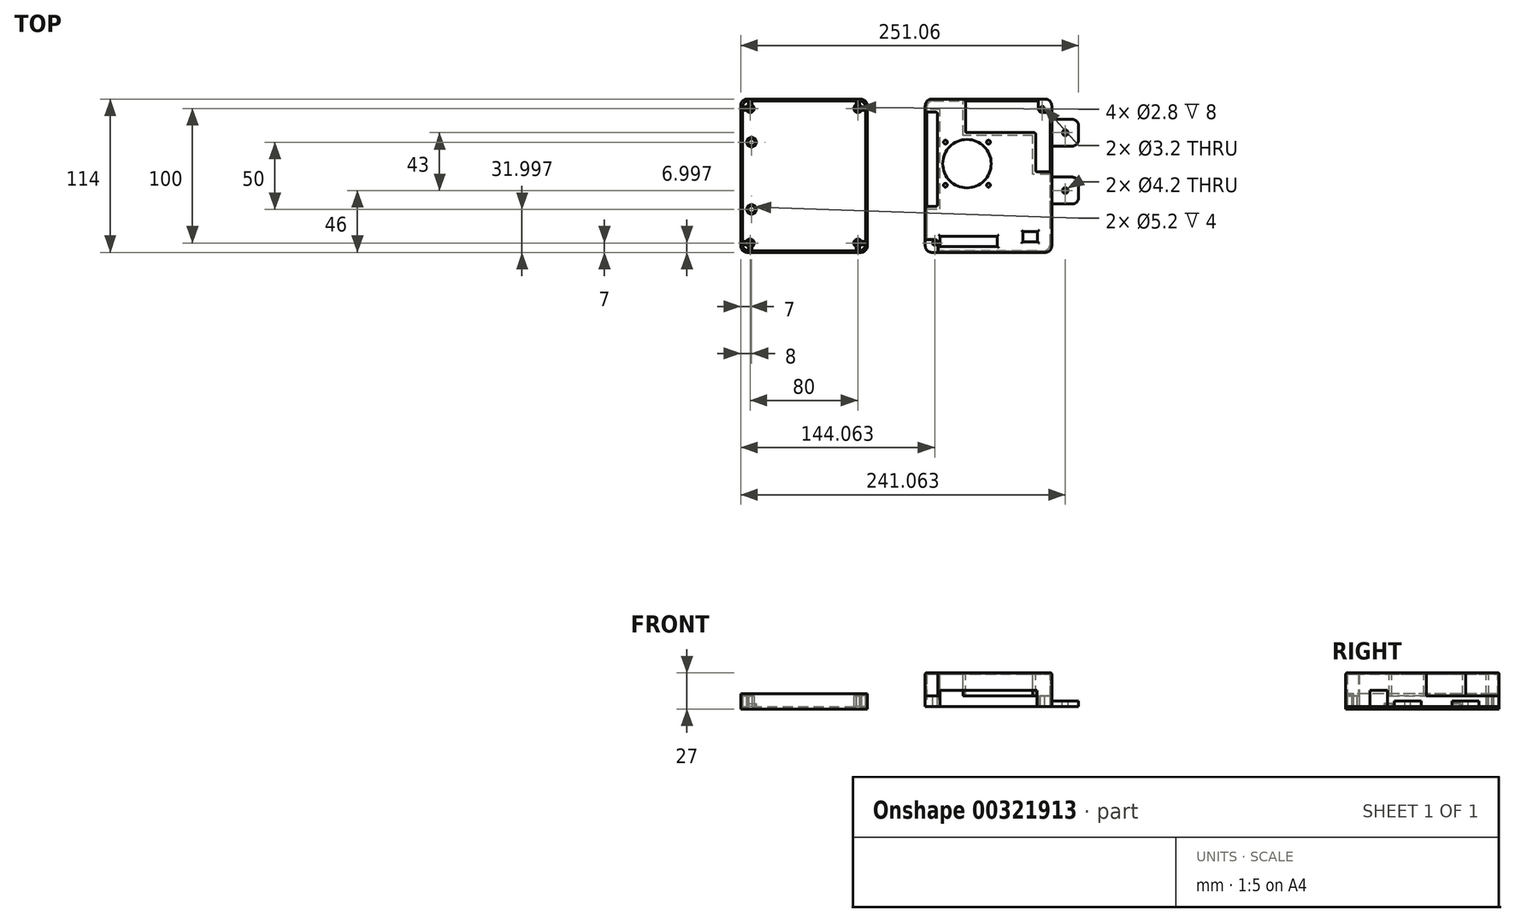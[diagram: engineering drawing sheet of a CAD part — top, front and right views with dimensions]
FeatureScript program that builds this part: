
annotation { "Feature Type Name" : "Feature", "Feature Type Description" : "" }
export const myFeature = defineFeature(function(context is Context, id is Id, definition is map)
    precondition{}
    {
        {
            var Q0;
            Q0=qCreatedBy(makeId("Top.planeOp"),FACE);
            var sketch = newSketch(context, id + "F0", { "sketchPlane" : qUnion([Q0])});
            skLineSegment(sketch, "E0.bottom", {"start": v(-88.3, 58.87) * mm, "end": v(5.7, 58.87) * mm});
            skLineSegment(sketch, "E0.top", {"start": v(-88.3, -55.13) * mm, "end": v(5.7, -55.13) * mm});
            skLineSegment(sketch, "E0.left", {"start": v(-88.3, 58.87) * mm, "end": v(-88.3, -55.13) * mm});
            skLineSegment(sketch, "E0.right", {"start": v(5.7, 58.87) * mm, "end": v(5.7, -55.13) * mm});
            skCircle(sketch, "E1", {"center": v(-81.3, 51.87) * mm, "radius": 1.4 * mm});
            skCircle(sketch, "E2", {"center": v(-81.3, -48.13) * mm, "radius": 1.4 * mm});
            skCircle(sketch, "E3", {"center": v(-1.3, -48.13) * mm, "radius": 1.4 * mm});
            skCircle(sketch, "E4", {"center": v(-1.3, 51.87) * mm, "radius": 1.4 * mm});
            skLineSegment(sketch, "E5", {"start": v(-87.1, 57.67) * mm, "end": v(4.5, 57.67) * mm});
            skLineSegment(sketch, "E6", {"start": v(-87.1, 57.67) * mm, "end": v(-87.1, -53.93) * mm});
            skLineSegment(sketch, "E7", {"start": v(-87.1, -53.93) * mm, "end": v(4.5, -53.93) * mm});
            skLineSegment(sketch, "E8", {"start": v(4.5, -53.93) * mm, "end": v(4.5, 57.67) * mm});
            skCircle(sketch, "E9", {"center": v(-81.3, 51.87) * mm, "radius": 3 * mm});
            skCircle(sketch, "E10", {"center": v(-1.3, 51.87) * mm, "radius": 3 * mm});
            skCircle(sketch, "E11", {"center": v(-81.3, -48.13) * mm, "radius": 3 * mm});
            skCircle(sketch, "E12", {"center": v(-1.3, -48.13) * mm, "radius": 3 * mm});
            skLineSegment(sketch, "E13", {"start": v(-87.1, 53.17) * mm, "end": v(-84, 53.17) * mm});
            skLineSegment(sketch, "E14", {"start": v(-87.1, 50.67) * mm, "end": v(-84, 50.67) * mm});
            skLineSegment(sketch, "E15", {"start": v(-82.6, 57.67) * mm, "end": v(-82.6, 54.57) * mm});
            skLineSegment(sketch, "E16", {"start": v(-80.1, 57.67) * mm, "end": v(-80.1, 54.62) * mm});
            skLineSegment(sketch, "E17", {"start": v(-2.5, 54.62) * mm, "end": v(-2.5, 57.67) * mm});
            skLineSegment(sketch, "E18", {"start": v(0, 57.67) * mm, "end": v(0, 54.57) * mm});
            skLineSegment(sketch, "E19", {"start": v(4.5, 53.17) * mm, "end": v(1.4, 53.17) * mm});
            skLineSegment(sketch, "E20", {"start": v(1.45, 50.67) * mm, "end": v(4.5, 50.67) * mm});
            skLineSegment(sketch, "E21", {"start": v(-87.1, -46.93) * mm, "end": v(-84.05, -46.93) * mm});
            skLineSegment(sketch, "E22", {"start": v(-87.1, -49.43) * mm, "end": v(-84, -49.43) * mm});
            skLineSegment(sketch, "E23", {"start": v(-82.6, -53.93) * mm, "end": v(-82.6, -50.84) * mm});
            skLineSegment(sketch, "E24", {"start": v(-80.1, -53.93) * mm, "end": v(-80.1, -50.88) * mm});
            skLineSegment(sketch, "E25", {"start": v(-2.5, -53.93) * mm, "end": v(-2.5, -50.88) * mm});
            skLineSegment(sketch, "E26", {"start": v(0, -53.93) * mm, "end": v(0, -50.84) * mm});
            skLineSegment(sketch, "E27", {"start": v(4.5, -49.43) * mm, "end": v(1.4, -49.43) * mm});
            skLineSegment(sketch, "E28", {"start": v(4.5, -46.93) * mm, "end": v(1.45, -46.93) * mm});
            skSolve(sketch);
        }
        {
            var Q0;
            Q0=makeQuery(id+"F0.imprint","IMPRINT",FACE,{"disambiguationData":[TD([[makeQuery(id+"F0.imprint","IMPRINT",EDGE,{"derivedFrom":sQuery(id+"F0.wireOp",EDGE,"E1")}),-1.0]])]});
            var Q1;
            Q1=makeQuery(id+"F0.imprint","IMPRINT",FACE,{"disambiguationData":[TD([[makeQuery(id+"F0.imprint","IMPRINT",EDGE,{"derivedFrom":sQuery(id+"F0.wireOp",EDGE,"E0.bottom")}),-1.0]])]});
            var Q2;
            Q2=makeQuery(id+"F0.imprint","IMPRINT",FACE,{"disambiguationData":[TD([[makeQuery(id+"F0.imprint","IMPRINT",EDGE,{"derivedFrom":sQuery(id+"F0.wireOp",EDGE,"E1")}),1.0]])]});
            var Q3;
            Q3=makeQuery(id+"F0.imprint","IMPRINT",FACE,{"disambiguationData":[TD([[makeQuery(id+"F0.imprint","IMPRINT",EDGE,{"derivedFrom":sQuery(id+"F0.wireOp",EDGE,"E4")}),1.0]])]});
            var Q4;
            Q4=makeQuery(id+"F0.imprint","IMPRINT",FACE,{"disambiguationData":[TD([[makeQuery(id+"F0.imprint","IMPRINT",EDGE,{"derivedFrom":sQuery(id+"F0.wireOp",EDGE,"E3")}),1.0]])]});
            var Q5;
            Q5=makeQuery(id+"F0.imprint","IMPRINT",FACE,{"disambiguationData":[TD([[makeQuery(id+"F0.imprint","IMPRINT",EDGE,{"derivedFrom":sQuery(id+"F0.wireOp",EDGE,"E2")}),1.0]])]});
            var Q6;
            Q6=makeQuery(id+"F0.imprint","IMPRINT",FACE,{"disambiguationData":[TD([[makeQuery(id+"F0.imprint","IMPRINT",EDGE,{"derivedFrom":sQuery(id+"F0.wireOp",EDGE,"E5")}),-1.0]])]});
            var Q7;
            Q7=makeQuery(id+"F0.imprint","IMPRINT",FACE,{"disambiguationData":[TD([[makeQuery(id+"F0.imprint","IMPRINT",EDGE,{"derivedFrom":sQuery(id+"F0.wireOp",EDGE,"E4")}),-1.0]])]});
            var Q8;
            Q8=makeQuery(id+"F0.imprint","IMPRINT",FACE,{"disambiguationData":[TD([[makeQuery(id+"F0.imprint","IMPRINT",EDGE,{"derivedFrom":sQuery(id+"F0.wireOp",EDGE,"E3")}),-1.0]])]});
            var Q9;
            Q9=makeQuery(id+"F0.imprint","IMPRINT",FACE,{"disambiguationData":[TD([[makeQuery(id+"F0.imprint","IMPRINT",EDGE,{"derivedFrom":sQuery(id+"F0.wireOp",EDGE,"E2")}),-1.0]])]});
            var Q10;
            {var subQ14=sQuery(id+"F0.wireOp",EDGE,"E16");Q10=makeQuery(id+"F0.imprint","IMPRINT",FACE,{"disambiguationData":[TD([[makeQuery(id+"F0.imprint","IMPRINT",EDGE,{"derivedFrom":subQ14}),1.0]])]});}
            var Q11;
            {var subQ0=sQuery(id+"F0.wireOp",EDGE,"E22");Q11=makeQuery(id+"F0.imprint","IMPRINT",FACE,{"disambiguationData":[TD([[makeQuery(id+"F0.imprint","IMPRINT",EDGE,{"derivedFrom":subQ0}),-1.0]])]});}
            var Q12;
            {var subQ0=sQuery(id+"F0.wireOp",EDGE,"E18");Q12=makeQuery(id+"F0.imprint","IMPRINT",FACE,{"disambiguationData":[TD([[makeQuery(id+"F0.imprint","IMPRINT",EDGE,{"derivedFrom":subQ0}),1.0]])]});}
            var Q13;
            {var subQ0=sQuery(id+"F0.wireOp",EDGE,"E19");Q13=makeQuery(id+"F0.imprint","IMPRINT",FACE,{"disambiguationData":[TD([[makeQuery(id+"F0.imprint","IMPRINT",EDGE,{"derivedFrom":subQ0}),1.0]])]});}
            var Q14;
            {var subQ0=sQuery(id+"F0.wireOp",EDGE,"E13");Q14=makeQuery(id+"F0.imprint","IMPRINT",FACE,{"disambiguationData":[TD([[makeQuery(id+"F0.imprint","IMPRINT",EDGE,{"derivedFrom":subQ0}),-1.0]])]});}
            var Q15;
            {var subQ0=sQuery(id+"F0.wireOp",EDGE,"E13");Q15=makeQuery(id+"F0.imprint","IMPRINT",FACE,{"disambiguationData":[TD([[makeQuery(id+"F0.imprint","IMPRINT",EDGE,{"derivedFrom":subQ0}),1.0]])]});}
            var Q16;
            {var subQ0=sQuery(id+"F0.wireOp",EDGE,"E23");Q16=makeQuery(id+"F0.imprint","IMPRINT",FACE,{"disambiguationData":[TD([[makeQuery(id+"F0.imprint","IMPRINT",EDGE,{"derivedFrom":subQ0}),-1.0]])]});}
            var Q17;
            {var subQ0=sQuery(id+"F0.wireOp",EDGE,"E21");Q17=makeQuery(id+"F0.imprint","IMPRINT",FACE,{"disambiguationData":[TD([[makeQuery(id+"F0.imprint","IMPRINT",EDGE,{"derivedFrom":subQ0}),-1.0]])]});}
            var Q18;
            {var subQ4=sQuery(id+"F0.wireOp",EDGE,"E26");Q18=makeQuery(id+"F0.imprint","IMPRINT",FACE,{"disambiguationData":[TD([[makeQuery(id+"F0.imprint","IMPRINT",EDGE,{"derivedFrom":subQ4}),-1.0]])]});}
            var Q19;
            {var subQ0=sQuery(id+"F0.wireOp",EDGE,"E25");Q19=makeQuery(id+"F0.imprint","IMPRINT",FACE,{"disambiguationData":[TD([[makeQuery(id+"F0.imprint","IMPRINT",EDGE,{"derivedFrom":subQ0}),-1.0]])]});}
            var Q20;
            {var subQ0=sQuery(id+"F0.wireOp",EDGE,"E27");Q20=makeQuery(id+"F0.imprint","IMPRINT",FACE,{"disambiguationData":[TD([[makeQuery(id+"F0.imprint","IMPRINT",EDGE,{"derivedFrom":subQ0}),-1.0]])]});}
            extrude(context, id + "F1", {"entities" : qUnion([Q0, Q1, Q2, Q3, Q4, Q5, Q6, Q7, Q8, Q9, Q10, Q11, Q12, Q13, Q14, Q15, Q16, Q17, Q18, Q19, Q20]), "oppositeDirection" : true, "depth" : 2 * mm, "offsetDistance" : 25 * mm});
        }
        {
            var Q0;
            Q0=makeQuery(id+"F0.imprint","IMPRINT",FACE,{"disambiguationData":[TD([[makeQuery(id+"F0.imprint","IMPRINT",EDGE,{"derivedFrom":sQuery(id+"F0.wireOp",EDGE,"E1")}),-1.0]])]});
            var Q1;
            Q1=makeQuery(id+"F0.imprint","IMPRINT",FACE,{"disambiguationData":[TD([[makeQuery(id+"F0.imprint","IMPRINT",EDGE,{"derivedFrom":sQuery(id+"F0.wireOp",EDGE,"E4")}),-1.0]])]});
            var Q2;
            Q2=makeQuery(id+"F0.imprint","IMPRINT",FACE,{"disambiguationData":[TD([[makeQuery(id+"F0.imprint","IMPRINT",EDGE,{"derivedFrom":sQuery(id+"F0.wireOp",EDGE,"E2")}),-1.0]])]});
            var Q3;
            Q3=makeQuery(id+"F0.imprint","IMPRINT",FACE,{"disambiguationData":[TD([[makeQuery(id+"F0.imprint","IMPRINT",EDGE,{"derivedFrom":sQuery(id+"F0.wireOp",EDGE,"E3")}),-1.0]])]});
            var Q4;
            {var subQ0=sQuery(id+"F0.wireOp",EDGE,"E13");Q4=makeQuery(id+"F0.imprint","IMPRINT",FACE,{"disambiguationData":[TD([[makeQuery(id+"F0.imprint","IMPRINT",EDGE,{"derivedFrom":subQ0}),-1.0]])]});}
            var Q5;
            {var subQ0=sQuery(id+"F0.wireOp",EDGE,"E15");Q5=makeQuery(id+"F0.imprint","IMPRINT",FACE,{"disambiguationData":[TD([[makeQuery(id+"F0.imprint","IMPRINT",EDGE,{"derivedFrom":subQ0}),1.0]])]});}
            var Q6;
            {var subQ0=sQuery(id+"F0.wireOp",EDGE,"E17");Q6=makeQuery(id+"F0.imprint","IMPRINT",FACE,{"disambiguationData":[TD([[makeQuery(id+"F0.imprint","IMPRINT",EDGE,{"derivedFrom":subQ0}),-1.0]])]});}
            var Q7;
            {var subQ0=sQuery(id+"F0.wireOp",EDGE,"E19");Q7=makeQuery(id+"F0.imprint","IMPRINT",FACE,{"disambiguationData":[TD([[makeQuery(id+"F0.imprint","IMPRINT",EDGE,{"derivedFrom":subQ0}),1.0]])]});}
            var Q8;
            {var subQ0=sQuery(id+"F0.wireOp",EDGE,"E27");Q8=makeQuery(id+"F0.imprint","IMPRINT",FACE,{"disambiguationData":[TD([[makeQuery(id+"F0.imprint","IMPRINT",EDGE,{"derivedFrom":subQ0}),-1.0]])]});}
            var Q9;
            {var subQ0=sQuery(id+"F0.wireOp",EDGE,"E25");Q9=makeQuery(id+"F0.imprint","IMPRINT",FACE,{"disambiguationData":[TD([[makeQuery(id+"F0.imprint","IMPRINT",EDGE,{"derivedFrom":subQ0}),-1.0]])]});}
            var Q10;
            {var subQ0=sQuery(id+"F0.wireOp",EDGE,"E23");Q10=makeQuery(id+"F0.imprint","IMPRINT",FACE,{"disambiguationData":[TD([[makeQuery(id+"F0.imprint","IMPRINT",EDGE,{"derivedFrom":subQ0}),-1.0]])]});}
            var Q11;
            {var subQ0=sQuery(id+"F0.wireOp",EDGE,"E21");Q11=makeQuery(id+"F0.imprint","IMPRINT",FACE,{"disambiguationData":[TD([[makeQuery(id+"F0.imprint","IMPRINT",EDGE,{"derivedFrom":subQ0}),-1.0]])]});}
            extrude(context, id + "F2", {"entities" : qUnion([Q0, Q1, Q2, Q3, Q4, Q5, Q6, Q7, Q8, Q9, Q10, Q11]), "operationType" : NewBodyOperationType.ADD, "depth" : 8 * mm, "offsetDistance" : 25 * mm});
        }
        {
            var Q0;
            Q0=makeQuery(id+"F0.imprint","IMPRINT",FACE,{"disambiguationData":[TD([[makeQuery(id+"F0.imprint","IMPRINT",EDGE,{"derivedFrom":sQuery(id+"F0.wireOp",EDGE,"E0.bottom")}),-1.0]])]});
            extrude(context, id + "F3", {"entities" : qUnion([Q0]), "operationType" : NewBodyOperationType.ADD, "offsetDistance" : 25 * mm, "depth" : 9.5 * mm});
        }
        {
            var Q0;
            Q0=makeQuery(id+"F3.opExtrude","SWEPT_EDGE",EDGE,{"disambiguationData":[OSD([sQuery(id+"F0.wireOp",EDGE,"E5"),sQuery(id+"F0.wireOp",EDGE,"E8")])]});
            var Q1;
            {var subQ0=sQuery(id+"F0.wireOp",EDGE,"E0.right");var subQ1=sQuery(id+"F0.wireOp",EDGE,"E0.bottom");Q1=makeQuery(id+"F3.boolean.opBoolean","MERGE",EDGE,{"derivedFrom":[makeQuery(id+"F1.opExtrude","SWEPT_EDGE",EDGE,{"disambiguationData":[OSD([subQ1,subQ0])]}),makeQuery(id+"F3.opExtrude","SWEPT_EDGE",EDGE,{"disambiguationData":[OSD([subQ1,subQ0])]})]});}
            var Q2;
            Q2=makeQuery(id+"F3.opExtrude","SWEPT_EDGE",EDGE,{"disambiguationData":[OSD([sQuery(id+"F0.wireOp",EDGE,"E5"),sQuery(id+"F0.wireOp",EDGE,"E6")])]});
            var Q3;
            {var subQ0=sQuery(id+"F0.wireOp",EDGE,"E0.left");var subQ1=sQuery(id+"F0.wireOp",EDGE,"E0.bottom");Q3=makeQuery(id+"F3.boolean.opBoolean","MERGE",EDGE,{"derivedFrom":[makeQuery(id+"F1.opExtrude","SWEPT_EDGE",EDGE,{"disambiguationData":[OSD([subQ1,subQ0])]}),makeQuery(id+"F3.opExtrude","SWEPT_EDGE",EDGE,{"disambiguationData":[OSD([subQ1,subQ0])]})]});}
            var Q4;
            Q4=makeQuery(id+"F3.opExtrude","SWEPT_EDGE",EDGE,{"disambiguationData":[OSD([sQuery(id+"F0.wireOp",EDGE,"E6"),sQuery(id+"F0.wireOp",EDGE,"E7")])]});
            var Q5;
            {var subQ0=sQuery(id+"F0.wireOp",EDGE,"E0.left");var subQ1=sQuery(id+"F0.wireOp",EDGE,"E0.top");Q5=makeQuery(id+"F3.boolean.opBoolean","MERGE",EDGE,{"derivedFrom":[makeQuery(id+"F1.opExtrude","SWEPT_EDGE",EDGE,{"disambiguationData":[OSD([subQ1,subQ0])]}),makeQuery(id+"F3.opExtrude","SWEPT_EDGE",EDGE,{"disambiguationData":[OSD([subQ1,subQ0])]})]});}
            var Q6;
            {var subQ0=sQuery(id+"F0.wireOp",EDGE,"E0.right");var subQ1=sQuery(id+"F0.wireOp",EDGE,"E0.top");Q6=makeQuery(id+"F3.boolean.opBoolean","MERGE",EDGE,{"derivedFrom":[makeQuery(id+"F1.opExtrude","SWEPT_EDGE",EDGE,{"disambiguationData":[OSD([subQ1,subQ0])]}),makeQuery(id+"F3.opExtrude","SWEPT_EDGE",EDGE,{"disambiguationData":[OSD([subQ1,subQ0])]})]});}
            var Q7;
            Q7=makeQuery(id+"F3.opExtrude","SWEPT_EDGE",EDGE,{"disambiguationData":[OSD([sQuery(id+"F0.wireOp",EDGE,"E7"),sQuery(id+"F0.wireOp",EDGE,"E8")])]});
            fillet(context, id + "F4", {"entities" : qUnion([Q0, Q1, Q2, Q3, Q4, Q5, Q6, Q7]), "radius" : 5 * mm, "tangentPropagation" : true, "allowEdgeOverflow" : false});
        }
        {
            var Q0;
            Q0=makeQuery(id+"F1.opExtrude","CAP_FACE",FACE,{"disambiguationData":[OSD([sQuery(id+"F0.wireOp",EDGE,"E0.bottom"),sQuery(id+"F0.wireOp",EDGE,"E0.top"),sQuery(id+"F0.wireOp",EDGE,"E0.left"),sQuery(id+"F0.wireOp",EDGE,"E0.right")])],"isStart":false});
            var sketch = newSketch(context, id + "F5", { "sketchPlane" : qUnion([Q0])});
            skCircle(sketch, "E29", {"center": v(-80.3, -26.87) * mm, "radius": 2.6 * mm});
            skCircle(sketch, "E30", {"center": v(-80.3, 23.13) * mm, "radius": 2.6 * mm});
            skCircle(sketch, "E31", {"center": v(-80.3, -26.87) * mm, "radius": 3.6 * mm});
            skCircle(sketch, "E32", {"center": v(-80.3, 23.13) * mm, "radius": 3.6 * mm});
            skSolve(sketch);
        }
        {
            var Q0;
            Q0=makeQuery(id+"F5.imprint","IMPRINT",FACE,{"disambiguationData":[TD([[makeQuery(id+"F5.imprint","IMPRINT",EDGE,{"derivedFrom":sQuery(id+"F5.wireOp",EDGE,"E29")}),1.0]])]});
            var Q1;
            Q1=makeQuery(id+"F5.imprint","IMPRINT",FACE,{"disambiguationData":[TD([[makeQuery(id+"F5.imprint","IMPRINT",EDGE,{"derivedFrom":sQuery(id+"F5.wireOp",EDGE,"E30")}),1.0]])]});
            extrude(context, id + "F6", {"entities" : qUnion([Q0, Q1]), "operationType" : NewBodyOperationType.REMOVE, "oppositeDirection" : true, "depth" : 25 * mm, "offsetDistance" : 25 * mm});
        }
        {
            var Q0;
            Q0=makeQuery(id+"F5.imprint","IMPRINT",FACE,{"disambiguationData":[TD([[makeQuery(id+"F5.imprint","IMPRINT",EDGE,{"derivedFrom":sQuery(id+"F5.wireOp",EDGE,"E29")}),-1.0]])]});
            var Q1;
            Q1=makeQuery(id+"F5.imprint","IMPRINT",FACE,{"disambiguationData":[TD([[makeQuery(id+"F5.imprint","IMPRINT",EDGE,{"derivedFrom":sQuery(id+"F5.wireOp",EDGE,"E30")}),-1.0]])]});
            extrude(context, id + "F7", {"entities" : qUnion([Q0, Q1]), "operationType" : NewBodyOperationType.ADD, "oppositeDirection" : true, "depth" : 4 * mm, "offsetDistance" : 25 * mm});
        }
        {
            var Q0;
            Q0=qCreatedBy(makeId("Top.planeOp"),FACE);
            var sketch = newSketch(context, id + "F8", { "sketchPlane" : qUnion([Q0])});
            skLineSegment(sketch, "E33.bottom", {"start": v(48.76, 58.87) * mm, "end": v(133.26, 58.87) * mm});
            skLineSegment(sketch, "E33.top", {"start": v(58.26, -55.13) * mm, "end": v(142.76, -55.13) * mm});
            skLineSegment(sketch, "E33.left", {"start": v(48.76, 58.87) * mm, "end": v(48.76, -45.63) * mm});
            skLineSegment(sketch, "E33.right", {"start": v(142.76, 49.37) * mm, "end": v(142.76, -55.13) * mm});
            skCircle(sketch, "E34", {"center": v(55.76, 51.87) * mm, "radius": 1.4 * mm});
            skCircle(sketch, "E35", {"center": v(55.76, -48.13) * mm, "radius": 1.6 * mm});
            skCircle(sketch, "E36", {"center": v(135.76, -48.13) * mm, "radius": 1.4 * mm});
            skCircle(sketch, "E37", {"center": v(135.76, 51.87) * mm, "radius": 1.6 * mm});
            skLineSegment(sketch, "E38", {"start": v(49.96, 57.67) * mm, "end": v(133.26, 57.67) * mm});
            skLineSegment(sketch, "E39", {"start": v(49.96, 57.67) * mm, "end": v(49.96, -45.63) * mm});
            skLineSegment(sketch, "E40", {"start": v(58.26, -53.93) * mm, "end": v(141.56, -53.93) * mm});
            skLineSegment(sketch, "E41", {"start": v(141.56, -53.93) * mm, "end": v(141.56, 49.37) * mm});
            skCircle(sketch, "E42", {"center": v(55.76, 51.87) * mm, "radius": 2.5 * mm});
            skArc(sketch, "E43", {"start": v(133.26, 51.87) * mm, "mid": v(134, 50.1) * mm, "end": v(135.76, 49.37) * mm});
            skCircle(sketch, "E44", {"center": v(55.76, -48.13) * mm, "radius": 2.5 * mm});
            skCircle(sketch, "E45", {"center": v(135.76, -48.13) * mm, "radius": 2.5 * mm});
            skLineSegment(sketch, "E46", {"start": v(58.26, -48.13) * mm, "end": v(58.26, -53.93) * mm});
            skLineSegment(sketch, "E47", {"start": v(55.76, -45.63) * mm, "end": v(49.96, -45.63) * mm});
            skLineSegment(sketch, "E48", {"start": v(133.26, 51.87) * mm, "end": v(133.26, 57.67) * mm});
            skLineSegment(sketch, "E49", {"start": v(135.76, 49.37) * mm, "end": v(141.56, 49.37) * mm});
            skPoint(sketch, "E50.orphan", {"position": v(141.56, 57.67) * mm});
            skLineSegment(sketch, "E51", {"start": v(133.26, 58.87) * mm, "end": v(142.76, 58.87) * mm});
            skLineSegment(sketch, "E52", {"start": v(142.76, 58.87) * mm, "end": v(142.76, 49.37) * mm});
            skLineSegment(sketch, "E53", {"start": v(141.56, 49.37) * mm, "end": v(141.56, 57.67) * mm});
            skLineSegment(sketch, "E54", {"start": v(141.56, 57.67) * mm, "end": v(133.26, 57.67) * mm});
            skLineSegment(sketch, "E55", {"start": v(48.76, -45.63) * mm, "end": v(48.76, -55.13) * mm});
            skLineSegment(sketch, "E56", {"start": v(48.76, -55.13) * mm, "end": v(58.26, -55.13) * mm});
            skLineSegment(sketch, "E57", {"start": v(58.26, -53.93) * mm, "end": v(49.96, -53.93) * mm});
            skLineSegment(sketch, "E58", {"start": v(49.96, -53.93) * mm, "end": v(49.96, -45.63) * mm});
            skLineSegment(sketch, "E59", {"start": v(141.56, 49.37) * mm, "end": v(142.76, 49.37) * mm});
            skLineSegment(sketch, "E60", {"start": v(133.26, 57.67) * mm, "end": v(133.26, 58.87) * mm});
            skLineSegment(sketch, "E61", {"start": v(49.96, -45.63) * mm, "end": v(48.76, -45.63) * mm});
            skLineSegment(sketch, "E62", {"start": v(58.26, -53.93) * mm, "end": v(58.26, -55.13) * mm});
            skSolve(sketch);
        }
        {
            var Q0;
            Q0=makeQuery(id+"F8.imprint","IMPRINT",FACE,{"disambiguationData":[TD([[makeQuery(id+"F8.imprint","IMPRINT",EDGE,{"derivedFrom":sQuery(id+"F8.wireOp",EDGE,"E33.bottom")}),-1.0]])]});
            var Q1;
            Q1=makeQuery(id+"F8.imprint","IMPRINT",FACE,{"disambiguationData":[TD([[makeQuery(id+"F8.imprint","IMPRINT",EDGE,{"derivedFrom":sQuery(id+"F8.wireOp",EDGE,"E34")}),-1.0]])]});
            var Q2;
            Q2=makeQuery(id+"F8.imprint","IMPRINT",FACE,{"disambiguationData":[TD([[makeQuery(id+"F8.imprint","IMPRINT",EDGE,{"derivedFrom":sQuery(id+"F8.wireOp",EDGE,"E34")}),1.0]])]});
            var Q3;
            Q3=makeQuery(id+"F8.imprint","IMPRINT",FACE,{"disambiguationData":[TD([[makeQuery(id+"F8.imprint","IMPRINT",EDGE,{"derivedFrom":sQuery(id+"F8.wireOp",EDGE,"E38")}),-1.0]])]});
            var Q4;
            Q4=makeQuery(id+"F8.imprint","IMPRINT",FACE,{"disambiguationData":[TD([[makeQuery(id+"F8.imprint","IMPRINT",EDGE,{"derivedFrom":sQuery(id+"F8.wireOp",EDGE,"E36")}),-1.0]])]});
            var Q5;
            Q5=makeQuery(id+"F8.imprint","IMPRINT",FACE,{"disambiguationData":[TD([[makeQuery(id+"F8.imprint","IMPRINT",EDGE,{"derivedFrom":sQuery(id+"F8.wireOp",EDGE,"E36")}),1.0]])]});
            var Q6;
            Q6=makeQuery(id+"F8.imprint","IMPRINT",FACE,{"disambiguationData":[TD([[makeQuery(id+"F8.imprint","IMPRINT",EDGE,{"derivedFrom":sQuery(id+"F8.wireOp",EDGE,"E33.top")}),1.0]])]});
            extrude(context, id + "F9", {"entities" : qUnion([Q0, Q1, Q2, Q3, Q4, Q5, Q6]), "depth" : 25 * mm});
        }
        {
            var Q0;
            Q0=makeQuery(id+"F8.imprint","IMPRINT",FACE,{"disambiguationData":[TD([[makeQuery(id+"F8.imprint","IMPRINT",EDGE,{"derivedFrom":sQuery(id+"F8.wireOp",EDGE,"E37")}),-1.0]])]});
            var Q1;
            Q1=makeQuery(id+"F8.imprint","IMPRINT",FACE,{"disambiguationData":[TD([[makeQuery(id+"F8.imprint","IMPRINT",EDGE,{"derivedFrom":sQuery(id+"F8.wireOp",EDGE,"E51")}),-1.0]])]});
            var Q2;
            {var subQ1=sQuery(id+"F8.wireOp",EDGE,"E46");Q2=makeQuery(id+"F8.imprint","IMPRINT",FACE,{"disambiguationData":[TD([[makeQuery(id+"F8.imprint","IMPRINT",EDGE,{"derivedFrom":subQ1}),-1.0]])]});}
            var Q3;
            Q3=makeQuery(id+"F8.imprint","IMPRINT",FACE,{"disambiguationData":[TD([[makeQuery(id+"F8.imprint","IMPRINT",EDGE,{"derivedFrom":sQuery(id+"F8.wireOp",EDGE,"E35")}),-1.0]])]});
            var Q4;
            Q4=makeQuery(id+"F8.imprint","IMPRINT",FACE,{"disambiguationData":[TD([[makeQuery(id+"F8.imprint","IMPRINT",EDGE,{"derivedFrom":sQuery(id+"F8.wireOp",EDGE,"E55")}),1.0]])]});
            extrude(context, id + "F10", {"entities" : qUnion([Q0, Q1, Q2, Q3, Q4]), "operationType" : NewBodyOperationType.ADD, "depth" : 8 * mm});
        }
        {
            var Q0;
            Q0=makeQuery(id+"F8.imprint","IMPRINT",FACE,{"disambiguationData":[TD([[makeQuery(id+"F8.imprint","IMPRINT",EDGE,{"derivedFrom":sQuery(id+"F8.wireOp",EDGE,"E38")}),-1.0]])]});
            var sketch = newSketch(context, id + "F11", { "sketchPlane" : qUnion([Q0])});
            skCircle(sketch, "E63", {"center": v(55.76, -48.13) * mm, "radius": 3 * mm});
            skLineSegment(sketch, "E64", {"start": v(58.76, -48.13) * mm, "end": v(58.76, -55.21) * mm});
            skLineSegment(sketch, "E65", {"start": v(55.76, -45.13) * mm, "end": v(48.76, -45.13) * mm});
            skCircle(sketch, "E66", {"center": v(135.76, 51.87) * mm, "radius": 3 * mm});
            skLineSegment(sketch, "E67", {"start": v(135.76, 48.87) * mm, "end": v(142.76, 48.87) * mm});
            skLineSegment(sketch, "E68", {"start": v(132.76, 51.87) * mm, "end": v(132.76, 58.87) * mm});
            skSolve(sketch);
        }
        {
            var Q0;
            Q0=makeQuery(id+"F11.imprint","IMPRINT",FACE,{"disambiguationData":[TD([[makeQuery(id+"F11.imprint","IMPRINT",EDGE,{"derivedFrom":makeQuery(id+"F8.imprint","IMPRINT",EDGE,{"derivedFrom":sQuery(id+"F8.wireOp",EDGE,"E42")})}),-1.0]])]});
            var Q1;
            Q1=makeQuery(id+"F11.imprint","IMPRINT",FACE,{"disambiguationData":[TD([[makeQuery(id+"F11.imprint","IMPRINT",EDGE,{"derivedFrom":makeQuery(id+"F8.imprint","IMPRINT",EDGE,{"derivedFrom":sQuery(id+"F8.wireOp",EDGE,"E45")})}),1.0]])]});
            var Q2;
            Q2=makeQuery(id+"F11.imprint","IMPRINT",FACE,{"disambiguationData":[TD([[makeQuery(id+"F11.imprint","IMPRINT",EDGE,{"derivedFrom":makeQuery(id+"F8.imprint","IMPRINT",EDGE,{"derivedFrom":sQuery(id+"F8.wireOp",EDGE,"E42")})}),1.0]])]});
            extrude(context, id + "F12", {"entities" : qUnion([Q0, Q1, Q2]), "operationType" : NewBodyOperationType.REMOVE, "depth" : 24 * mm});
        }
        {
            var Q0;
            Q0=makeQuery(id+"F12.boolean.opBoolean","COPY",EDGE,{"derivedFrom":makeQuery(id+"F12.opExtrude","SWEPT_EDGE",EDGE,{"disambiguationData":[OSD([sQuery(id+"F8.wireOp",EDGE,"E38"),sQuery(id+"F8.wireOp",EDGE,"E39")])]})});
            var Q1;
            Q1=makeQuery(id+"F12.boolean.opBoolean","COPY",EDGE,{"derivedFrom":makeQuery(id+"F12.opExtrude","SWEPT_EDGE",EDGE,{"disambiguationData":[OSD([sQuery(id+"F8.wireOp",EDGE,"E40"),sQuery(id+"F8.wireOp",EDGE,"E41")])]})});
            var Q2;
            Q2=makeQuery(id+"F10.opExtrude","SWEPT_EDGE",EDGE,{"disambiguationData":[OSD([sQuery(id+"F8.wireOp",EDGE,"E51"),sQuery(id+"F8.wireOp",EDGE,"E52")])]});
            var Q3;
            Q3=makeQuery(id+"F9.opExtrude","SWEPT_EDGE",EDGE,{"disambiguationData":[OSD([sQuery(id+"F8.wireOp",EDGE,"E33.top"),sQuery(id+"F8.wireOp",EDGE,"E33.right")])]});
            var Q4;
            Q4=makeQuery(id+"F10.opExtrude","SWEPT_EDGE",EDGE,{"disambiguationData":[OSD([sQuery(id+"F8.wireOp",EDGE,"E55"),sQuery(id+"F8.wireOp",EDGE,"E56")])]});
            var Q5;
            Q5=makeQuery(id+"F9.opExtrude","SWEPT_EDGE",EDGE,{"disambiguationData":[OSD([sQuery(id+"F8.wireOp",EDGE,"E33.bottom"),sQuery(id+"F8.wireOp",EDGE,"E33.left")])]});
            fillet(context, id + "F13", {"entities" : qUnion([Q0, Q1, Q2, Q3, Q4, Q5]), "radius" : 5 * mm, "tangentPropagation" : true, "allowEdgeOverflow" : false});
        }
        {
            var Q0;
            Q0=makeQuery(id+"F10.boolean.opBoolean","MERGE",FACE,{"derivedFrom":[makeQuery(id+"F9.opExtrude","SWEPT_FACE",FACE,{"disambiguationData":[OSD([sQuery(id+"F8.wireOp",EDGE,"E33.top")])]}),makeQuery(id+"F10.opExtrude","SWEPT_FACE",FACE,{"disambiguationData":[OSD([sQuery(id+"F8.wireOp",EDGE,"E56")])]})]});
            var sketch = newSketch(context, id + "F14", { "sketchPlane" : qUnion([Q0])});
            skLineSegment(sketch, "E69", {"start": v(59.76, 12) * mm, "end": v(131.76, 12) * mm});
            skLineSegment(sketch, "E70", {"start": v(59.76, 12) * mm, "end": v(59.76, 0) * mm});
            skLineSegment(sketch, "E71", {"start": v(131.76, 12) * mm, "end": v(131.76, 0) * mm});
            skSolve(sketch);
        }
        {
            var Q0;
            Q0=makeQuery(id+"F14.imprint","IMPRINT",FACE,{"disambiguationData":[TD([[makeQuery(id+"F14.imprint","IMPRINT",EDGE,{"derivedFrom":sQuery(id+"F14.wireOp",EDGE,"E69")}),-1.0]])]});
            extrude(context, id + "F15", {"entities" : qUnion([Q0]), "operationType" : NewBodyOperationType.REMOVE, "oppositeDirection" : true, "depth" : 2 * mm});
        }
        {
            var Q0;
            Q0=makeQuery(id+"F9.opExtrude","CAP_FACE",FACE,{"disambiguationData":[OSD([sQuery(id+"F8.wireOp",EDGE,"E33.bottom"),sQuery(id+"F8.wireOp",EDGE,"E33.top"),sQuery(id+"F8.wireOp",EDGE,"E33.left"),sQuery(id+"F8.wireOp",EDGE,"E33.right"),sQuery(id+"F8.wireOp",EDGE,"E43"),sQuery(id+"F8.wireOp",EDGE,"E44"),sQuery(id+"F8.wireOp",EDGE,"E46"),sQuery(id+"F8.wireOp",EDGE,"E47"),sQuery(id+"F8.wireOp",EDGE,"E48"),sQuery(id+"F8.wireOp",EDGE,"E49"),sQuery(id+"F8.wireOp",EDGE,"E59"),sQuery(id+"F8.wireOp",EDGE,"E60"),sQuery(id+"F8.wireOp",EDGE,"E61"),sQuery(id+"F8.wireOp",EDGE,"E62")])],"isStart":false});
            var sketch = newSketch(context, id + "F16", { "sketchPlane" : qUnion([Q0])});
            skLineSegment(sketch, "E72.bottom", {"start": v(59.76, -43.13) * mm, "end": v(102.26, -43.13) * mm});
            skLineSegment(sketch, "E72.top", {"start": v(59.76, -50.63) * mm, "end": v(102.26, -50.63) * mm});
            skLineSegment(sketch, "E72.left", {"start": v(59.76, -43.13) * mm, "end": v(59.76, -50.63) * mm});
            skLineSegment(sketch, "E72.right", {"start": v(102.26, -43.13) * mm, "end": v(102.26, -50.63) * mm});
            skLineSegment(sketch, "E73.bottom", {"start": v(121.26, -39.63) * mm, "end": v(132.26, -39.63) * mm});
            skLineSegment(sketch, "E73.top", {"start": v(121.26, -47.13) * mm, "end": v(132.26, -47.13) * mm});
            skLineSegment(sketch, "E73.left", {"start": v(121.26, -39.63) * mm, "end": v(121.26, -47.13) * mm});
            skLineSegment(sketch, "E73.right", {"start": v(132.26, -39.63) * mm, "end": v(132.26, -47.13) * mm});
            skLineSegment(sketch, "E74.bottom", {"start": v(48.76, 49.12) * mm, "end": v(57.76, 49.12) * mm});
            skLineSegment(sketch, "E74.top", {"start": v(48.76, -20.88) * mm, "end": v(57.76, -20.88) * mm});
            skLineSegment(sketch, "E74.left", {"start": v(48.76, 49.12) * mm, "end": v(48.76, -20.88) * mm});
            skLineSegment(sketch, "E74.right", {"start": v(57.76, 49.12) * mm, "end": v(57.76, -20.88) * mm});
            skLineSegment(sketch, "E75", {"start": v(130.76, 33.87) * mm, "end": v(78.76, 33.87) * mm});
            skLineSegment(sketch, "E76", {"start": v(78.76, 33.87) * mm, "end": v(78.76, 58.87) * mm});
            skLineSegment(sketch, "E77", {"start": v(130.76, 33.87) * mm, "end": v(130.76, 4.87) * mm});
            skLineSegment(sketch, "E78", {"start": v(130.76, 4.87) * mm, "end": v(142.76, 4.87) * mm});
            skCircle(sketch, "E79", {"center": v(63.76, -5.13) * mm, "radius": 1.4 * mm});
            skCircle(sketch, "E80", {"center": v(63.76, 26.87) * mm, "radius": 1.4 * mm});
            skCircle(sketch, "E81", {"center": v(95.76, 26.87) * mm, "radius": 1.4 * mm});
            skCircle(sketch, "E82", {"center": v(95.76, -5.13) * mm, "radius": 1.4 * mm});
            skPoint(sketch, "E83", {"position": v(79.76, 10.87) * mm});
            skCircle(sketch, "E84", {"center": v(79.76, 10.87) * mm, "radius": 18 * mm});
            skSolve(sketch);
        }
        {
            var Q0;
            Q0=makeQuery(id+"F16.imprint","IMPRINT",FACE,{"disambiguationData":[TD([[makeQuery(id+"F16.imprint","IMPRINT",EDGE,{"derivedFrom":sQuery(id+"F16.wireOp",EDGE,"E74.bottom")}),-1.0]])]});
            var Q1;
            Q1=makeQuery(id+"F16.imprint","IMPRINT",FACE,{"disambiguationData":[TD([[makeQuery(id+"F16.imprint","IMPRINT",EDGE,{"derivedFrom":sQuery(id+"F16.wireOp",EDGE,"E75")}),-1.0]])]});
            var Q2;
            Q2=makeQuery(id+"F16.imprint","IMPRINT",FACE,{"disambiguationData":[TD([[makeQuery(id+"F16.imprint","IMPRINT",EDGE,{"derivedFrom":sQuery(id+"F16.wireOp",EDGE,"E72.bottom")}),-1.0]])]});
            var Q3;
            Q3=makeQuery(id+"F16.imprint","IMPRINT",FACE,{"disambiguationData":[TD([[makeQuery(id+"F16.imprint","IMPRINT",EDGE,{"derivedFrom":sQuery(id+"F16.wireOp",EDGE,"E73.bottom")}),-1.0]])]});
            var Q4;
            Q4=makeQuery(id+"F16.imprint","IMPRINT",FACE,{"disambiguationData":[TD([[makeQuery(id+"F16.imprint","IMPRINT",EDGE,{"derivedFrom":sQuery(id+"F16.wireOp",EDGE,"E84")}),1.0]])]});
            var Q5;
            Q5=makeQuery(id+"F16.imprint","IMPRINT",FACE,{"disambiguationData":[TD([[makeQuery(id+"F16.imprint","IMPRINT",EDGE,{"derivedFrom":sQuery(id+"F16.wireOp",EDGE,"E79")}),1.0]])]});
            var Q6;
            Q6=makeQuery(id+"F16.imprint","IMPRINT",FACE,{"disambiguationData":[TD([[makeQuery(id+"F16.imprint","IMPRINT",EDGE,{"derivedFrom":sQuery(id+"F16.wireOp",EDGE,"E82")}),1.0]])]});
            var Q7;
            Q7=makeQuery(id+"F16.imprint","IMPRINT",FACE,{"disambiguationData":[TD([[makeQuery(id+"F16.imprint","IMPRINT",EDGE,{"derivedFrom":sQuery(id+"F16.wireOp",EDGE,"E81")}),1.0]])]});
            var Q8;
            Q8=makeQuery(id+"F16.imprint","IMPRINT",FACE,{"disambiguationData":[TD([[makeQuery(id+"F16.imprint","IMPRINT",EDGE,{"derivedFrom":sQuery(id+"F16.wireOp",EDGE,"E80")}),1.0]])]});
            extrude(context, id + "F17", {"entities" : qUnion([Q0, Q1, Q2, Q3, Q4, Q5, Q6, Q7, Q8]), "operationType" : NewBodyOperationType.REMOVE, "oppositeDirection" : true, "depth" : 17 * mm});
        }
        {
            var Q0;
            Q0=makeQuery(id+"F10.boolean.opBoolean","MERGE",FACE,{"derivedFrom":[makeQuery(id+"F9.opExtrude","SWEPT_FACE",FACE,{"disambiguationData":[OSD([sQuery(id+"F8.wireOp",EDGE,"E33.right")])]}),makeQuery(id+"F10.opExtrude","SWEPT_FACE",FACE,{"disambiguationData":[OSD([sQuery(id+"F8.wireOp",EDGE,"E52")])]})]});
            var sketch = newSketch(context, id + "F18", { "sketchPlane" : qUnion([Q0])});
            skLineSegment(sketch, "E85", {"start": v(-37.13, 0) * mm, "end": v(-37.13, 12) * mm});
            skLineSegment(sketch, "E86", {"start": v(-37.13, 12) * mm, "end": v(-24.13, 12) * mm});
            skLineSegment(sketch, "E87", {"start": v(-24.13, 12) * mm, "end": v(-24.13, 0) * mm});
            skSolve(sketch);
        }
        {
            var Q0;
            {var subQ0=sQuery(id+"F18.wireOp",EDGE,"E85");Q0=makeQuery(id+"F18.imprint","IMPRINT",FACE,{"disambiguationData":[TD([[makeQuery(id+"F18.imprint","IMPRINT",EDGE,{"derivedFrom":subQ0}),-1.0]])]});}
            extrude(context, id + "F19", {"entities" : qUnion([Q0]), "operationType" : NewBodyOperationType.REMOVE, "oppositeDirection" : true, "depth" : 3 * mm});
        }
        {
            var Q0;
            Q0=makeQuery(id+"F12.boolean.opBoolean","COPY",FACE,{"derivedFrom":makeQuery(id+"F12.opExtrude","CAP_FACE",FACE,{"disambiguationData":[OSD([sQuery(id+"F8.wireOp",EDGE,"E38"),sQuery(id+"F8.wireOp",EDGE,"E39"),sQuery(id+"F8.wireOp",EDGE,"E40"),sQuery(id+"F8.wireOp",EDGE,"E41"),sQuery(id+"F11.wireOp",EDGE,"E63"),sQuery(id+"F11.wireOp",EDGE,"E64"),sQuery(id+"F11.wireOp",EDGE,"E65"),sQuery(id+"F11.wireOp",EDGE,"E66"),sQuery(id+"F11.wireOp",EDGE,"E67"),sQuery(id+"F11.wireOp",EDGE,"E68")])],"isStart":false})});
            var sketch = newSketch(context, id + "F20", { "sketchPlane" : qUnion([Q0])});
            skLineSegment(sketch, "E88", {"start": v(141.56, -2.87) * mm, "end": v(128.76, -2.87) * mm});
            skLineSegment(sketch, "E89", {"start": v(128.76, -2.87) * mm, "end": v(128.76, -31.87) * mm});
            skLineSegment(sketch, "E90", {"start": v(128.76, -31.87) * mm, "end": v(76.76, -31.87) * mm});
            skLineSegment(sketch, "E91", {"start": v(76.76, -31.87) * mm, "end": v(76.76, -57.67) * mm});
            skLineSegment(sketch, "E92", {"start": v(49.96, 22.88) * mm, "end": v(59.76, 22.88) * mm});
            skLineSegment(sketch, "E93", {"start": v(59.76, 22.88) * mm, "end": v(59.76, -51.12) * mm});
            skLineSegment(sketch, "E94", {"start": v(59.76, -51.12) * mm, "end": v(49.96, -51.12) * mm});
            skSolve(sketch);
        }
        {
            var Q0;
            {var subQ6=sQuery(id+"F20.wireOp",EDGE,"E88");Q0=makeQuery(id+"F20.imprint","IMPRINT",FACE,{"disambiguationData":[TD([[makeQuery(id+"F20.imprint","IMPRINT",EDGE,{"derivedFrom":subQ6}),1.0]])]});}
            var Q1;
            {var subQ13=sQuery(id+"F20.wireOp",EDGE,"E92");Q1=makeQuery(id+"F20.imprint","IMPRINT",FACE,{"disambiguationData":[TD([[makeQuery(id+"F20.imprint","IMPRINT",EDGE,{"derivedFrom":subQ13}),-1.0]])]});}
            extrude(context, id + "F21", {"entities" : qUnion([Q0, Q1]), "operationType" : NewBodyOperationType.ADD, "depth" : 16 * mm});
        }
        {
            var Q0;
            Q0=makeQuery(id+"F10.boolean.opBoolean","MERGE",FACE,{"derivedFrom":[makeQuery(id+"F9.opExtrude","SWEPT_FACE",FACE,{"disambiguationData":[OSD([sQuery(id+"F8.wireOp",EDGE,"E33.right")])]}),makeQuery(id+"F10.opExtrude","SWEPT_FACE",FACE,{"disambiguationData":[OSD([sQuery(id+"F8.wireOp",EDGE,"E52")])]})]});
            var sketch = newSketch(context, id + "F22", { "sketchPlane" : qUnion([Q0])});
            skLineSegment(sketch, "E95", {"start": v(-19.13, 0) * mm, "end": v(-19.13, 4) * mm});
            skLineSegment(sketch, "E96", {"start": v(-19.13, 4) * mm, "end": v(0.87, 4) * mm});
            skLineSegment(sketch, "E97", {"start": v(0.87, 4) * mm, "end": v(0.87, 0) * mm});
            skLineSegment(sketch, "E98", {"start": v(23.87, 0) * mm, "end": v(23.87, 4) * mm});
            skLineSegment(sketch, "E99", {"start": v(23.87, 4) * mm, "end": v(43.87, 4) * mm});
            skLineSegment(sketch, "E100", {"start": v(43.87, 4) * mm, "end": v(43.87, 0) * mm});
            skSolve(sketch);
        }
        {
            var Q0;
            {var subQ0=sQuery(id+"F22.wireOp",EDGE,"E95");Q0=makeQuery(id+"F22.imprint","IMPRINT",FACE,{"disambiguationData":[TD([[makeQuery(id+"F22.imprint","IMPRINT",EDGE,{"derivedFrom":subQ0}),-1.0]])]});}
            var Q1;
            {var subQ0=sQuery(id+"F22.wireOp",EDGE,"E98");Q1=makeQuery(id+"F22.imprint","IMPRINT",FACE,{"disambiguationData":[TD([[makeQuery(id+"F22.imprint","IMPRINT",EDGE,{"derivedFrom":subQ0}),-1.0]])]});}
            extrude(context, id + "F23", {"entities" : qUnion([Q0, Q1]), "operationType" : NewBodyOperationType.ADD, "depth" : 20 * mm});
        }
        {
            var Q0;
            Q0=makeQuery(id+"F23.opExtrude","SWEPT_FACE",FACE,{"disambiguationData":[OSD([sQuery(id+"F22.wireOp",EDGE,"E96")])]});
            var sketch = newSketch(context, id + "F24", { "sketchPlane" : qUnion([Q0])});
            skCircle(sketch, "E101", {"center": v(152.76, -9.13) * mm, "radius": 2.1 * mm});
            skPoint(sketch, "E101.centerSnap0", {"position": v(152.76, 0.87) * mm});
            skPoint(sketch, "E101.centerSnap1", {"position": v(162.76, -9.13) * mm});
            skCircle(sketch, "E102", {"center": v(152.76, 33.87) * mm, "radius": 2.1 * mm});
            skSolve(sketch);
        }
        {
            var Q0;
            Q0=makeQuery(id+"F24.imprint","IMPRINT",FACE,{"disambiguationData":[TD([[makeQuery(id+"F24.imprint","IMPRINT",EDGE,{"derivedFrom":sQuery(id+"F24.wireOp",EDGE,"E101")}),1.0]])]});
            var Q1;
            Q1=makeQuery(id+"F24.imprint","IMPRINT",FACE,{"disambiguationData":[TD([[makeQuery(id+"F24.imprint","IMPRINT",EDGE,{"derivedFrom":sQuery(id+"F24.wireOp",EDGE,"E102")}),1.0]])]});
            extrude(context, id + "F25", {"entities" : qUnion([Q0, Q1]), "operationType" : NewBodyOperationType.REMOVE, "endBound" : BoundingType.THROUGH_ALL, "oppositeDirection" : true, "depth" : 25 * mm});
        }
        {
            var Q0;
            Q0=makeQuery(id+"F17.boolean.opBoolean","COPY",EDGE,{"derivedFrom":makeQuery(id+"F17.opExtrude","SWEPT_EDGE",EDGE,{"disambiguationData":[OSD([sQuery(id+"F8.wireOp",EDGE,"E33.right"),sQuery(id+"F16.wireOp",EDGE,"E78")])]})});
            var Q1;
            {var subQ0=sQuery(id+"F16.wireOp",EDGE,"E77");var subQ1=sQuery(id+"F16.wireOp",EDGE,"E75");Q1=makeQuery(id+"F21.boolean.opBoolean","MERGE",EDGE,{"derivedFrom":[makeQuery(id+"F17.boolean.opBoolean","COPY",EDGE,{"derivedFrom":makeQuery(id+"F17.opExtrude","SWEPT_EDGE",EDGE,{"disambiguationData":[OSD([subQ1,subQ0])]})}),makeQuery(id+"F21.opExtrude","SWEPT_EDGE",EDGE,{"disambiguationData":[OSD([sQuery(id+"F8.wireOp",EDGE,"E38"),sQuery(id+"F8.wireOp",EDGE,"E39"),sQuery(id+"F8.wireOp",EDGE,"E40"),sQuery(id+"F8.wireOp",EDGE,"E41"),sQuery(id+"F11.wireOp",EDGE,"E63"),sQuery(id+"F11.wireOp",EDGE,"E64"),sQuery(id+"F11.wireOp",EDGE,"E65"),sQuery(id+"F11.wireOp",EDGE,"E66"),sQuery(id+"F11.wireOp",EDGE,"E67"),sQuery(id+"F11.wireOp",EDGE,"E68"),subQ1,subQ0])]})]});}
            var Q2;
            {var subQ0=sQuery(id+"F16.wireOp",EDGE,"E78");var subQ1=sQuery(id+"F16.wireOp",EDGE,"E77");Q2=makeQuery(id+"F21.boolean.opBoolean","MERGE",EDGE,{"derivedFrom":[makeQuery(id+"F17.boolean.opBoolean","COPY",EDGE,{"derivedFrom":makeQuery(id+"F17.opExtrude","SWEPT_EDGE",EDGE,{"disambiguationData":[OSD([subQ1,subQ0])]})}),makeQuery(id+"F21.opExtrude","SWEPT_EDGE",EDGE,{"disambiguationData":[OSD([sQuery(id+"F8.wireOp",EDGE,"E38"),sQuery(id+"F8.wireOp",EDGE,"E39"),sQuery(id+"F8.wireOp",EDGE,"E40"),sQuery(id+"F8.wireOp",EDGE,"E41"),sQuery(id+"F11.wireOp",EDGE,"E63"),sQuery(id+"F11.wireOp",EDGE,"E64"),sQuery(id+"F11.wireOp",EDGE,"E65"),sQuery(id+"F11.wireOp",EDGE,"E66"),sQuery(id+"F11.wireOp",EDGE,"E67"),sQuery(id+"F11.wireOp",EDGE,"E68"),subQ1,subQ0])]})]});}
            var Q3;
            {var subQ0=sQuery(id+"F16.wireOp",EDGE,"E76");var subQ1=sQuery(id+"F16.wireOp",EDGE,"E75");Q3=makeQuery(id+"F21.boolean.opBoolean","MERGE",EDGE,{"derivedFrom":[makeQuery(id+"F17.boolean.opBoolean","COPY",EDGE,{"derivedFrom":makeQuery(id+"F17.opExtrude","SWEPT_EDGE",EDGE,{"disambiguationData":[OSD([subQ1,subQ0])]})}),makeQuery(id+"F21.opExtrude","SWEPT_EDGE",EDGE,{"disambiguationData":[OSD([sQuery(id+"F8.wireOp",EDGE,"E38"),sQuery(id+"F8.wireOp",EDGE,"E39"),sQuery(id+"F8.wireOp",EDGE,"E40"),sQuery(id+"F8.wireOp",EDGE,"E41"),sQuery(id+"F11.wireOp",EDGE,"E63"),sQuery(id+"F11.wireOp",EDGE,"E64"),sQuery(id+"F11.wireOp",EDGE,"E65"),sQuery(id+"F11.wireOp",EDGE,"E66"),sQuery(id+"F11.wireOp",EDGE,"E67"),sQuery(id+"F11.wireOp",EDGE,"E68"),subQ1,subQ0])]})]});}
            var Q4;
            Q4=makeQuery(id+"F17.boolean.opBoolean","COPY",EDGE,{"derivedFrom":makeQuery(id+"F17.opExtrude","SWEPT_EDGE",EDGE,{"disambiguationData":[OSD([sQuery(id+"F8.wireOp",EDGE,"E33.bottom"),sQuery(id+"F16.wireOp",EDGE,"E76")])]})});
            var Q5;
            {var subQ0=sQuery(id+"F16.wireOp",EDGE,"E74.right");var subQ1=sQuery(id+"F16.wireOp",EDGE,"E74.top");Q5=makeQuery(id+"F21.boolean.opBoolean","MERGE",EDGE,{"derivedFrom":[makeQuery(id+"F17.boolean.opBoolean","COPY",EDGE,{"derivedFrom":makeQuery(id+"F17.opExtrude","SWEPT_EDGE",EDGE,{"disambiguationData":[OSD([subQ1,subQ0])]})}),makeQuery(id+"F21.opExtrude","SWEPT_EDGE",EDGE,{"disambiguationData":[OSD([sQuery(id+"F8.wireOp",EDGE,"E38"),sQuery(id+"F8.wireOp",EDGE,"E39"),sQuery(id+"F8.wireOp",EDGE,"E40"),sQuery(id+"F8.wireOp",EDGE,"E41"),sQuery(id+"F11.wireOp",EDGE,"E63"),sQuery(id+"F11.wireOp",EDGE,"E64"),sQuery(id+"F11.wireOp",EDGE,"E65"),sQuery(id+"F11.wireOp",EDGE,"E66"),sQuery(id+"F11.wireOp",EDGE,"E67"),sQuery(id+"F11.wireOp",EDGE,"E68"),subQ1,subQ0])]})]});}
            var Q6;
            Q6=makeQuery(id+"F17.boolean.opBoolean","COPY",EDGE,{"derivedFrom":makeQuery(id+"F17.opExtrude","SWEPT_EDGE",EDGE,{"disambiguationData":[OSD([sQuery(id+"F8.wireOp",EDGE,"E33.left"),sQuery(id+"F16.wireOp",EDGE,"E74.top"),sQuery(id+"F16.wireOp",EDGE,"E74.left")])]})});
            var Q7;
            Q7=makeQuery(id+"F9.opExtrude","SWEPT_EDGE",EDGE,{"disambiguationData":[OSD([sQuery(id+"F8.wireOp",EDGE,"E33.left"),sQuery(id+"F8.wireOp",EDGE,"E55"),sQuery(id+"F8.wireOp",EDGE,"E61")])]});
            var Q8;
            Q8=makeQuery(id+"F9.opExtrude","SWEPT_EDGE",EDGE,{"disambiguationData":[OSD([sQuery(id+"F8.wireOp",EDGE,"E33.top"),sQuery(id+"F8.wireOp",EDGE,"E56"),sQuery(id+"F8.wireOp",EDGE,"E62")])]});
            var Q9;
            Q9=makeQuery(id+"F9.opExtrude","CAP_FACE",FACE,{"disambiguationData":[OSD([sQuery(id+"F8.wireOp",EDGE,"E33.bottom"),sQuery(id+"F8.wireOp",EDGE,"E33.top"),sQuery(id+"F8.wireOp",EDGE,"E33.left"),sQuery(id+"F8.wireOp",EDGE,"E33.right"),sQuery(id+"F8.wireOp",EDGE,"E43"),sQuery(id+"F8.wireOp",EDGE,"E44"),sQuery(id+"F8.wireOp",EDGE,"E46"),sQuery(id+"F8.wireOp",EDGE,"E47"),sQuery(id+"F8.wireOp",EDGE,"E48"),sQuery(id+"F8.wireOp",EDGE,"E49"),sQuery(id+"F8.wireOp",EDGE,"E59"),sQuery(id+"F8.wireOp",EDGE,"E60"),sQuery(id+"F8.wireOp",EDGE,"E61"),sQuery(id+"F8.wireOp",EDGE,"E62")])],"isStart":false});
            var Q10;
            Q10=makeQuery(id+"F23.opExtrude","CAP_EDGE",EDGE,{"disambiguationData":[OSD([sQuery(id+"F22.wireOp",EDGE,"E96")])],"isStart":true});
            var Q11;
            Q11=makeQuery(id+"F23.opExtrude","CAP_EDGE",EDGE,{"disambiguationData":[OSD([sQuery(id+"F22.wireOp",EDGE,"E99")])],"isStart":true});
            var Q12;
            Q12=makeQuery(id+"F23.opExtrude","CAP_EDGE",EDGE,{"disambiguationData":[OSD([sQuery(id+"F22.wireOp",EDGE,"E97")])],"isStart":true});
            var Q13;
            Q13=makeQuery(id+"F23.opExtrude","CAP_EDGE",EDGE,{"disambiguationData":[OSD([sQuery(id+"F22.wireOp",EDGE,"E95")])],"isStart":true});
            var Q14;
            Q14=makeQuery(id+"F23.opExtrude","CAP_EDGE",EDGE,{"disambiguationData":[OSD([sQuery(id+"F22.wireOp",EDGE,"E100")])],"isStart":true});
            var Q15;
            Q15=makeQuery(id+"F23.opExtrude","CAP_EDGE",EDGE,{"disambiguationData":[OSD([sQuery(id+"F22.wireOp",EDGE,"E98")])],"isStart":true});
            var Q16;
            {var subQ0=sQuery(id+"F16.wireOp",EDGE,"E74.right");var subQ1=sQuery(id+"F16.wireOp",EDGE,"E74.bottom");Q16=makeQuery(id+"F21.boolean.opBoolean","MERGE",EDGE,{"derivedFrom":[makeQuery(id+"F17.boolean.opBoolean","COPY",EDGE,{"derivedFrom":makeQuery(id+"F17.opExtrude","SWEPT_EDGE",EDGE,{"disambiguationData":[OSD([subQ1,subQ0])]})}),makeQuery(id+"F21.opExtrude","SWEPT_EDGE",EDGE,{"disambiguationData":[OSD([sQuery(id+"F8.wireOp",EDGE,"E38"),sQuery(id+"F8.wireOp",EDGE,"E39"),sQuery(id+"F8.wireOp",EDGE,"E40"),sQuery(id+"F8.wireOp",EDGE,"E41"),sQuery(id+"F11.wireOp",EDGE,"E63"),sQuery(id+"F11.wireOp",EDGE,"E64"),sQuery(id+"F11.wireOp",EDGE,"E65"),sQuery(id+"F11.wireOp",EDGE,"E66"),sQuery(id+"F11.wireOp",EDGE,"E67"),sQuery(id+"F11.wireOp",EDGE,"E68"),subQ1,subQ0])]})]});}
            fillet(context, id + "F26", {"entities" : qUnion([Q0, Q1, Q2, Q3, Q4, Q5, Q6, Q7, Q8, Q9, Q10, Q11, Q12, Q13, Q14, Q15, Q16]), "radius" : 1 * mm, "tangentPropagation" : true, "allowEdgeOverflow" : false});
        }
        {
            var Q0;
            Q0=makeQuery(id+"F23.opExtrude","CAP_EDGE",EDGE,{"disambiguationData":[OSD([sQuery(id+"F22.wireOp",EDGE,"E95")])],"isStart":false});
            var Q1;
            Q1=makeQuery(id+"F23.opExtrude","CAP_EDGE",EDGE,{"disambiguationData":[OSD([sQuery(id+"F22.wireOp",EDGE,"E97")])],"isStart":false});
            var Q2;
            Q2=makeQuery(id+"F23.opExtrude","CAP_EDGE",EDGE,{"disambiguationData":[OSD([sQuery(id+"F22.wireOp",EDGE,"E98")])],"isStart":false});
            var Q3;
            Q3=makeQuery(id+"F23.opExtrude","CAP_EDGE",EDGE,{"disambiguationData":[OSD([sQuery(id+"F22.wireOp",EDGE,"E100")])],"isStart":false});
            fillet(context, id + "F27", {"entities" : qUnion([Q0, Q1, Q2, Q3]), "radius" : 5 * mm, "tangentPropagation" : true, "allowEdgeOverflow" : false});
        }
    });
